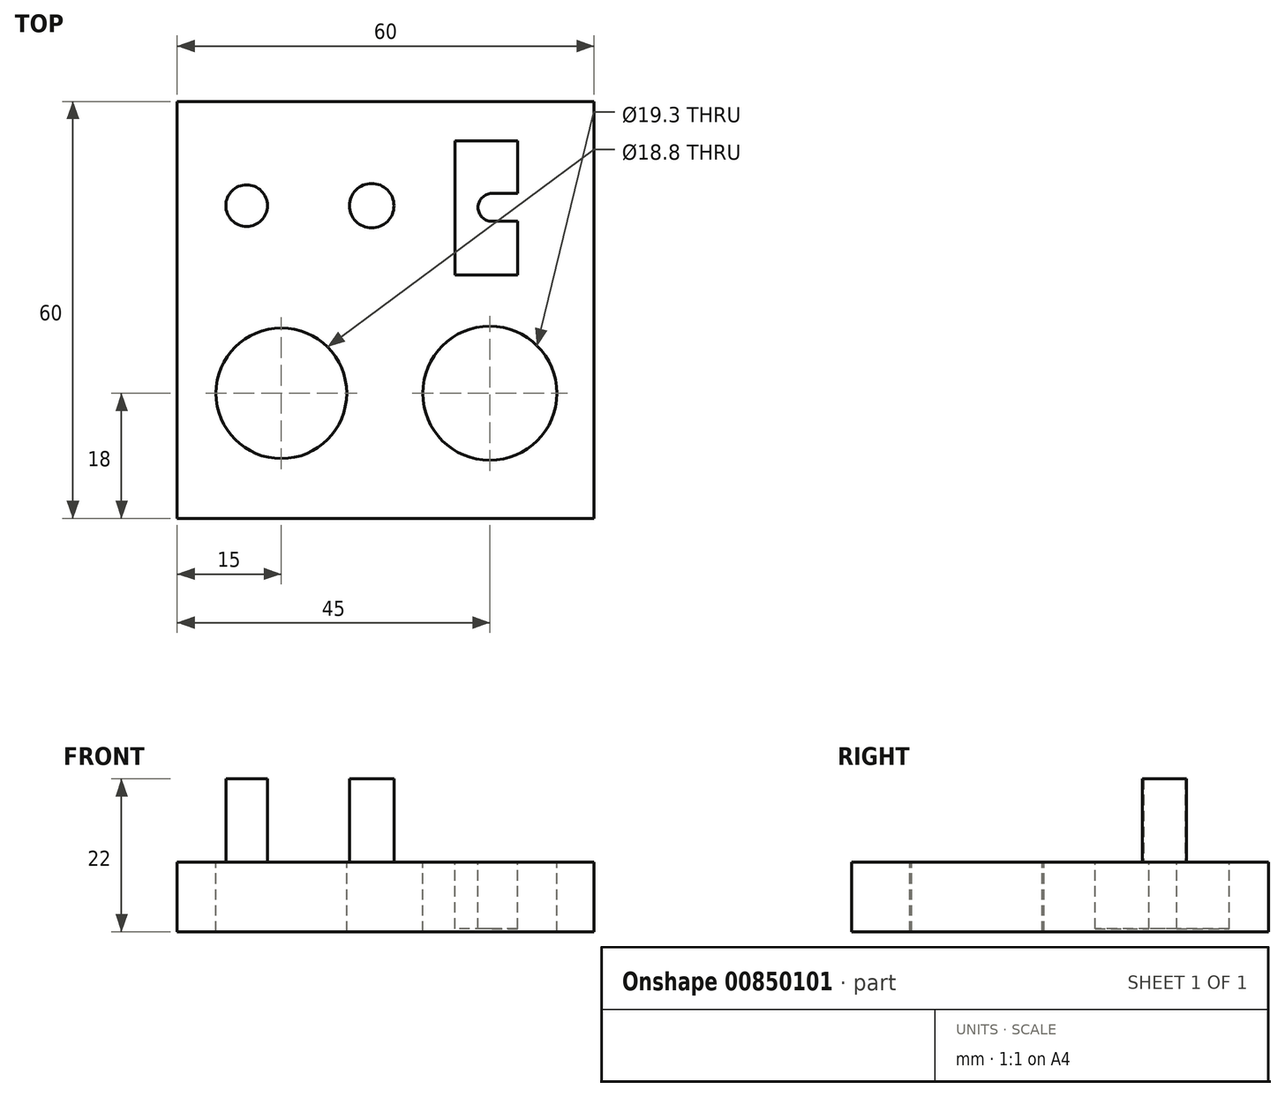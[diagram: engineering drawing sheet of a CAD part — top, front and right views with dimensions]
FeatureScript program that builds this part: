
annotation { "Feature Type Name" : "Feature", "Feature Type Description" : "" }
export const myFeature = defineFeature(function(context is Context, id is Id, definition is map)
    precondition{}
    {
        {
            var Q0;
            Q0=qCreatedBy(makeId("Top.planeOp"),FACE);
            var sketch = newSketch(context, id + "F0", { "sketchPlane" : qUnion([Q0])});
            skLineSegment(sketch, "E0.bottom", {"start": v(-30, 30) * mm, "end": v(30, 30) * mm});
            skLineSegment(sketch, "E0.top", {"start": v(-30, -30) * mm, "end": v(30, -30) * mm});
            skLineSegment(sketch, "E0.left", {"start": v(-30, 30) * mm, "end": v(-30, -30) * mm});
            skLineSegment(sketch, "E0.right", {"start": v(30, 30) * mm, "end": v(30, -30) * mm});
            skSolve(sketch);
        }
        {
            var Q0;
            Q0=makeQuery(id+"F0.imprint","IMPRINT",FACE,{"disambiguationData":[TD([[makeQuery(id+"F0.imprint","IMPRINT",EDGE,{"derivedFrom":sQuery(id+"F0.wireOp",EDGE,"E0.bottom")}),-1.0]])]});
            extrude(context, id + "F1", {"entities" : qUnion([Q0]), "depth" : 10 * mm, "offsetDistance" : 25 * mm});
        }
        {
            var Q0;
            Q0=makeQuery(id+"F1.opExtrude","CAP_FACE",FACE,{"disambiguationData":[OSD([sQuery(id+"F0.wireOp",EDGE,"E0.bottom"),sQuery(id+"F0.wireOp",EDGE,"E0.top"),sQuery(id+"F0.wireOp",EDGE,"E0.left"),sQuery(id+"F0.wireOp",EDGE,"E0.right")])],"isStart":false});
            var sketch = newSketch(context, id + "F2", { "sketchPlane" : qUnion([Q0])});
            skCircle(sketch, "E1", {"center": v(-20, 15) * mm, "radius": 3 * mm});
            skCircle(sketch, "E2", {"center": v(-2, 15) * mm, "radius": 3.2 * mm});
            skSolve(sketch);
        }
        {
            var Q0;
            Q0 = qSketchRegion(id + "F2", true);
            extrude(context, id + "F3", {"entities" : qUnion([Q0]), "operationType" : NewBodyOperationType.ADD, "depth" : 12 * mm, "offsetDistance" : 25 * mm});
        }
        {
            var Q0;
            Q0=makeQuery(id+"F1.opExtrude","CAP_FACE",FACE,{"disambiguationData":[OSD([sQuery(id+"F0.wireOp",EDGE,"E0.bottom"),sQuery(id+"F0.wireOp",EDGE,"E0.top"),sQuery(id+"F0.wireOp",EDGE,"E0.left"),sQuery(id+"F0.wireOp",EDGE,"E0.right")])],"isStart":false});
            var sketch = newSketch(context, id + "F4", { "sketchPlane" : qUnion([Q0])});
            skCircle(sketch, "E3", {"center": v(-15, -12) * mm, "radius": 9.4 * mm});
            skCircle(sketch, "E4", {"center": v(15, -12) * mm, "radius": 9.65 * mm});
            skSolve(sketch);
        }
        {
            var Q0;
            Q0=makeQuery(id+"F4.imprint","IMPRINT",FACE,{"disambiguationData":[TD([[makeQuery(id+"F4.imprint","IMPRINT",EDGE,{"derivedFrom":sQuery(id+"F4.wireOp",EDGE,"E3")}),1.0]])]});
            var Q1;
            Q1=makeQuery(id+"F4.imprint","IMPRINT",FACE,{"disambiguationData":[TD([[makeQuery(id+"F4.imprint","IMPRINT",EDGE,{"derivedFrom":sQuery(id+"F4.wireOp",EDGE,"E4")}),1.0]])]});
            extrude(context, id + "F5", {"entities" : qUnion([Q0, Q1]), "operationType" : NewBodyOperationType.REMOVE, "endBound" : BoundingType.UP_TO_NEXT, "oppositeDirection" : true, "depth" : 25 * mm, "offsetDistance" : 25 * mm});
        }
        {
            var Q0;
            Q0=makeQuery(id+"F1.opExtrude","CAP_FACE",FACE,{"disambiguationData":[OSD([sQuery(id+"F0.wireOp",EDGE,"E0.bottom"),sQuery(id+"F0.wireOp",EDGE,"E0.top"),sQuery(id+"F0.wireOp",EDGE,"E0.left"),sQuery(id+"F0.wireOp",EDGE,"E0.right")])],"isStart":false});
            var sketch = newSketch(context, id + "F6", { "sketchPlane" : qUnion([Q0])});
            skLineSegment(sketch, "E5", {"start": v(10, 24.3) * mm, "end": v(10, 5) * mm});
            skLineSegment(sketch, "E6", {"start": v(10, 5) * mm, "end": v(19, 5) * mm});
            skLineSegment(sketch, "E7", {"start": v(19, 5) * mm, "end": v(19, 12.75) * mm});
            skLineSegment(sketch, "E8", {"start": v(19, 12.75) * mm, "end": v(15.3, 12.75) * mm});
            skLineSegment(sketch, "E9", {"start": v(15.3, 16.75) * mm, "end": v(19, 16.75) * mm});
            skLineSegment(sketch, "E10", {"start": v(19, 16.75) * mm, "end": v(19, 24.3) * mm});
            skLineSegment(sketch, "E11", {"start": v(19, 24.3) * mm, "end": v(10, 24.3) * mm});
            skArc(sketch, "E12", {"start": v(15.3, 16.75) * mm, "mid": v(13.3, 14.75) * mm, "end": v(15.3, 12.75) * mm});
            skSolve(sketch);
        }
        {
            var Q0;
            Q0 = qSketchRegion(id + "F6", true);
            extrude(context, id + "F7", {"entities" : qUnion([Q0]), "operationType" : NewBodyOperationType.REMOVE, "oppositeDirection" : true, "depth" : 9.55 * mm, "offsetDistance" : 25 * mm});
        }
    });
